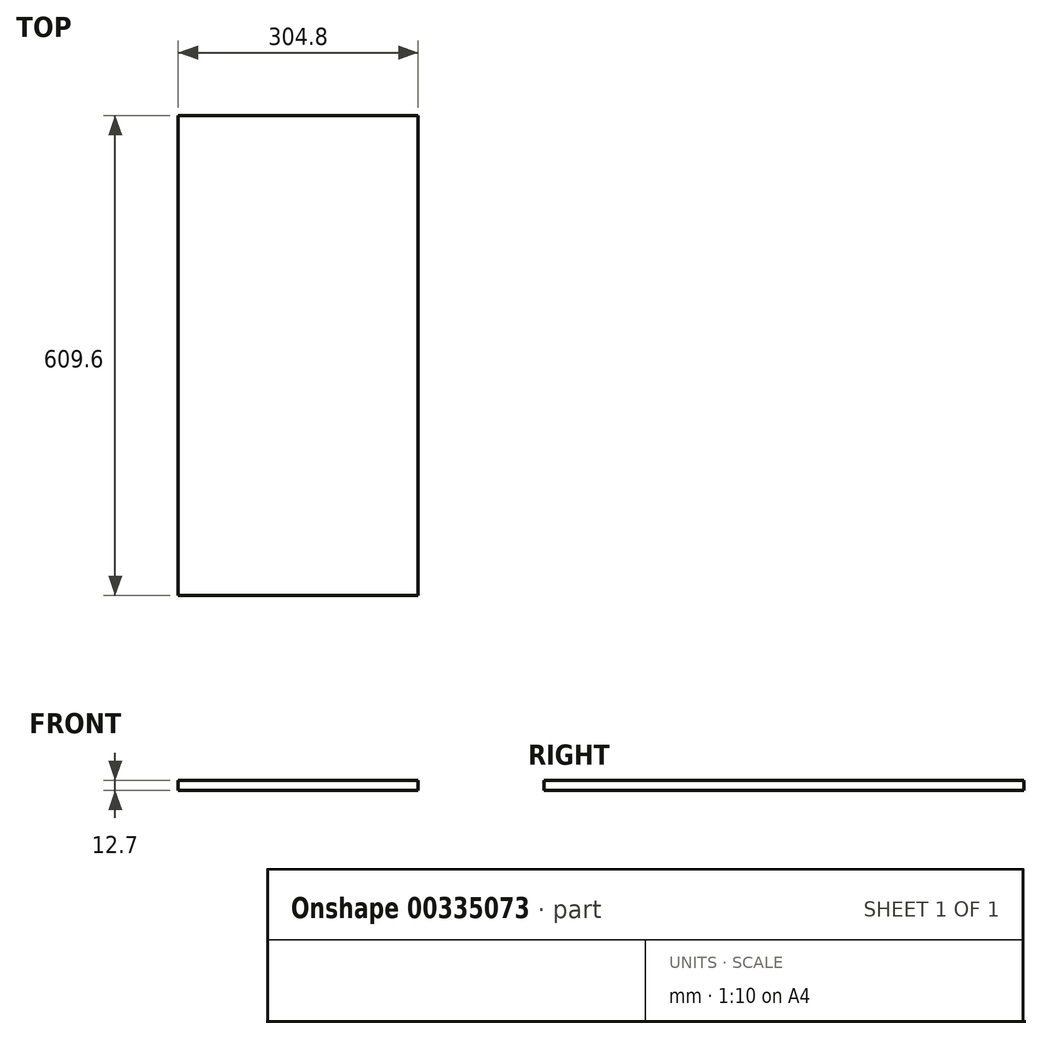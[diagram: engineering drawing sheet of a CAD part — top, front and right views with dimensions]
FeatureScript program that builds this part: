
annotation { "Feature Type Name" : "Feature", "Feature Type Description" : "" }
export const myFeature = defineFeature(function(context is Context, id is Id, definition is map)
    precondition{}
    {
        {
            var Q0;
            Q0=qCreatedBy(makeId("Top.planeOp"),FACE);
            var sketch = newSketch(context, id + "F0", { "sketchPlane" : qUnion([Q0])});
            skLineSegment(sketch, "E0", {"start": v(0, 0) * mm, "end": v(0, 609.6) * mm});
            skLineSegment(sketch, "E1", {"start": v(0, 609.6) * mm, "end": v(304.8, 609.6) * mm});
            skLineSegment(sketch, "E2", {"start": v(304.8, 0) * mm, "end": v(304.8, 609.6) * mm});
            skLineSegment(sketch, "E3", {"start": v(304.8, 0) * mm, "end": v(0, 0) * mm});
            skSolve(sketch);
        }
        {
            var Q0;
            Q0 = qSketchRegion(id + "F0", true);
            extrude(context, id + "F1", {"entities" : qUnion([Q0]), "depth" : 12.7 * mm});
        }
    });
